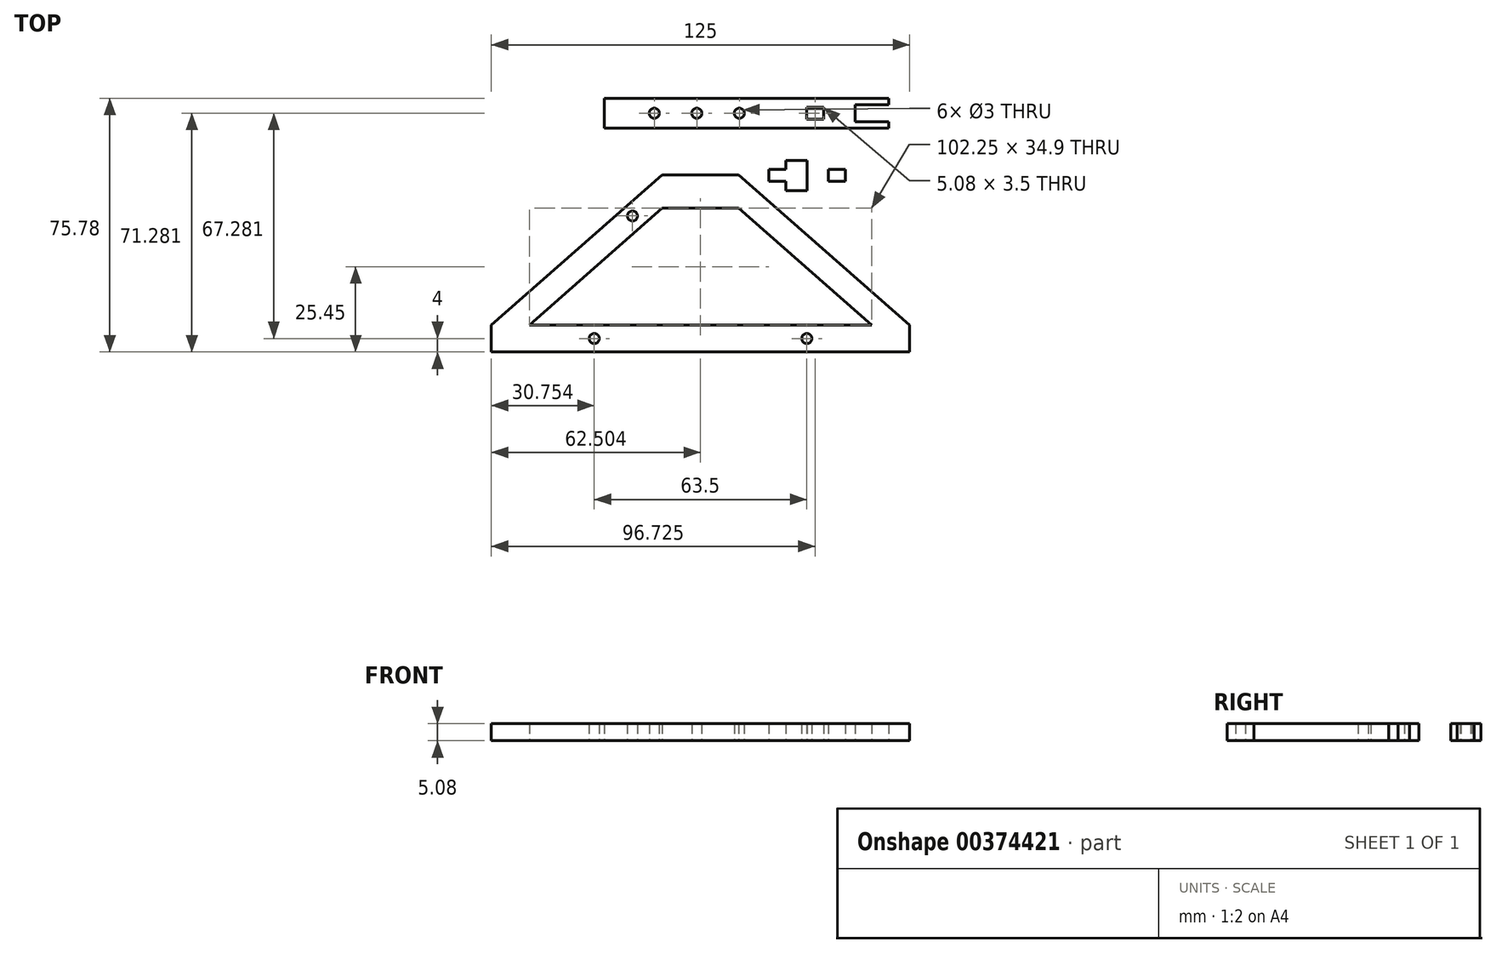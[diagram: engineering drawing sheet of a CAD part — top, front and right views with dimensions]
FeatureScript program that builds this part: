
annotation { "Feature Type Name" : "Feature", "Feature Type Description" : "" }
export const myFeature = defineFeature(function(context is Context, id is Id, definition is map)
    precondition{}
    {
        {
            var Q0;
            Q0=qCreatedBy(makeId("Top.planeOp"),FACE);
            var sketch = newSketch(context, id + "F0", { "sketchPlane" : qUnion([Q0])});
            skLineSegment(sketch, "E0.bottom", {"start": v(5, 50.75) * mm, "end": v(-80, 50.75) * mm});
            skLineSegment(sketch, "E0.top", {"start": v(5, 41.75) * mm, "end": v(-80, 41.75) * mm});
            skLineSegment(sketch, "E0.left", {"start": v(5, 50.75) * mm, "end": v(5, 41.75) * mm});
            skLineSegment(sketch, "E0.right", {"start": v(-80, 50.75) * mm, "end": v(-80, 41.75) * mm});
            skCircle(sketch, "E1", {"center": v(-65, 46.25) * mm, "radius": 1.5 * mm});
            skPoint(sketch, "E1.centerSnap0", {"position": v(-80, 46.25) * mm});
            skCircle(sketch, "E2", {"center": v(-39.6, 46.25) * mm, "radius": 1.5 * mm});
            skCircle(sketch, "E3", {"center": v(-52.3, 46.25) * mm, "radius": 1.5 * mm});
            skLineSegment(sketch, "E4.bottom", {"start": v(5, 48.8) * mm, "end": v(-5, 48.8) * mm});
            skLineSegment(sketch, "E4.top", {"start": v(5, 43.71) * mm, "end": v(-5, 43.71) * mm});
            skLineSegment(sketch, "E4.left", {"start": v(5, 48.8) * mm, "end": v(5, 43.71) * mm});
            skLineSegment(sketch, "E4.right", {"start": v(-5, 48.8) * mm, "end": v(-5, 43.71) * mm});
            skPoint(sketch, "E5.middle", {"position": v(-88.96, 46.25) * mm});
            skLineSegment(sketch, "E6.bottom", {"start": v(-19.52, 48) * mm, "end": v(-14.44, 48) * mm});
            skLineSegment(sketch, "E6.top", {"start": v(-19.52, 44.5) * mm, "end": v(-14.44, 44.5) * mm});
            skLineSegment(sketch, "E6.left", {"start": v(-19.52, 48) * mm, "end": v(-19.52, 44.5) * mm});
            skLineSegment(sketch, "E6.right", {"start": v(-14.44, 48) * mm, "end": v(-14.44, 44.5) * mm});
            skLineSegment(sketch, "E7.bottom", {"start": v(-25.75, 32.2) * mm, "end": v(-13.04, 32.2) * mm});
            skLineSegment(sketch, "E7.top", {"start": v(-25.75, 23.2) * mm, "end": v(-13.04, 23.2) * mm});
            skLineSegment(sketch, "E7.left", {"start": v(-25.75, 32.2) * mm, "end": v(-25.75, 23.2) * mm});
            skLineSegment(sketch, "E7.right", {"start": v(-13.04, 32.2) * mm, "end": v(-13.04, 23.2) * mm});
            skLineSegment(sketch, "E8.bottom", {"start": v(-13.04, 29.44) * mm, "end": v(-7.96, 29.44) * mm});
            skLineSegment(sketch, "E8.top", {"start": v(-13.04, 25.94) * mm, "end": v(-7.96, 25.94) * mm});
            skLineSegment(sketch, "E8.left", {"start": v(-13.04, 29.44) * mm, "end": v(-13.04, 25.94) * mm});
            skLineSegment(sketch, "E8.right", {"start": v(-7.96, 29.44) * mm, "end": v(-7.96, 25.94) * mm});
            skLineSegment(sketch, "E9", {"start": v(-19.4, 32.2) * mm, "end": v(-19.4, 23.2) * mm});
            skLineSegment(sketch, "E10.MirrorCS", {"start": v(-25.75, 29.44) * mm, "end": v(-30.83, 29.44) * mm});
            skLineSegment(sketch, "E11.MirrorCS", {"start": v(-30.83, 29.44) * mm, "end": v(-30.83, 25.94) * mm});
            skLineSegment(sketch, "E12.MirrorCS", {"start": v(-25.75, 25.94) * mm, "end": v(-30.83, 25.94) * mm});
            skLineSegment(sketch, "E13.bottom", {"start": v(-62.64, 27.87) * mm, "end": v(-39.77, 27.87) * mm});
            skLineSegment(sketch, "E13.top", {"start": v(-62.64, 17.87) * mm, "end": v(-39.77, 17.87) * mm});
            skLineSegment(sketch, "E13.left", {"start": v(-62.64, 27.87) * mm, "end": v(-62.64, 17.87) * mm});
            skLineSegment(sketch, "E13.right", {"start": v(-39.77, 27.87) * mm, "end": v(-39.77, 17.87) * mm});
            skLineSegment(sketch, "E14", {"start": v(-113.7, -17.03) * mm, "end": v(11.3, -17.03) * mm});
            skLineSegment(sketch, "E15", {"start": v(-113.7, -17.03) * mm, "end": v(-113.7, -25.03) * mm});
            skLineSegment(sketch, "E16", {"start": v(-113.7, -25.03) * mm, "end": v(11.3, -25.03) * mm});
            skLineSegment(sketch, "E17", {"start": v(11.3, -25.03) * mm, "end": v(11.3, -17.03) * mm});
            skCircle(sketch, "E18", {"center": v(-82.96, -21.03) * mm, "radius": 1.5 * mm});
            skPoint(sketch, "E18.centerSnap0", {"position": v(-113.7, -21.03) * mm});
            skCircle(sketch, "E19", {"center": v(-19.46, -21.03) * mm, "radius": 1.5 * mm});
            skLineSegment(sketch, "E20", {"start": v(-113.7, -17.03) * mm, "end": v(-62.64, 27.87) * mm});
            skLineSegment(sketch, "E21", {"start": v(-62.64, 17.87) * mm, "end": v(-102.33, -17.03) * mm});
            skLineSegment(sketch, "E22", {"start": v(-51.2, 27.87) * mm, "end": v(-51.2, -25.03) * mm});
            skLineSegment(sketch, "E23.MirrorCS", {"start": v(11.3, -17.03) * mm, "end": v(-39.77, 27.87) * mm});
            skLineSegment(sketch, "E24.MirrorCS", {"start": v(-39.77, 17.87) * mm, "end": v(-0.08, -17.03) * mm});
            skCircle(sketch, "E25", {"center": v(-71.53, 15.58) * mm, "radius": 1.5 * mm});
            skLineSegment(sketch, "E26", {"start": v(-62.64, 22.87) * mm, "end": v(-71.53, 15.58) * mm});
            skSolve(sketch);
        }
        {
            var Q0;
            Q0=makeQuery(id+"F0.imprint","IMPRINT",FACE,{"disambiguationData":[TD([[makeQuery(id+"F0.imprint","IMPRINT",EDGE,{"derivedFrom":sQuery(id+"F0.wireOp",EDGE,"E0.bottom")}),1.0]])]});
            var Q1;
            {var subQ6=sQuery(id+"F0.wireOp",EDGE,"E9");Q1=makeQuery(id+"F0.imprint","IMPRINT",FACE,{"disambiguationData":[TD([[makeQuery(id+"F0.imprint","IMPRINT",EDGE,{"derivedFrom":subQ6}),-1.0]])]});}
            var Q2;
            {var subQ0=sQuery(id+"F0.wireOp",EDGE,"E10.MirrorCS");Q2=makeQuery(id+"F0.imprint","IMPRINT",FACE,{"disambiguationData":[TD([[makeQuery(id+"F0.imprint","IMPRINT",EDGE,{"derivedFrom":subQ0}),1.0]])]});}
            var Q3;
            {var subQ3=sQuery(id+"F0.wireOp",EDGE,"E8.left");Q3=makeQuery(id+"F0.imprint","IMPRINT",FACE,{"disambiguationData":[TD([[makeQuery(id+"F0.imprint","IMPRINT",EDGE,{"derivedFrom":subQ3}),-1.0]])]});}
            var Q4;
            Q4=makeQuery(id+"F0.imprint","IMPRINT",FACE,{"disambiguationData":[TD([[makeQuery(id+"F0.imprint","IMPRINT",EDGE,{"derivedFrom":sQuery(id+"F0.wireOp",EDGE,"E8.bottom")}),-1.0]])]});
            var Q5;
            Q5=makeQuery(id+"F0.imprint","IMPRINT",FACE,{"disambiguationData":[TD([[makeQuery(id+"F0.imprint","IMPRINT",EDGE,{"derivedFrom":sQuery(id+"F0.wireOp",EDGE,"E13.bottom")}),-1.0]])]});
            var Q6;
            Q6=makeQuery(id+"F0.imprint","IMPRINT",FACE,{"disambiguationData":[TD([[makeQuery(id+"F0.imprint","IMPRINT",EDGE,{"derivedFrom":sQuery(id+"F0.wireOp",EDGE,"acEFhCEI-yFbl-H2Pa-5wQp-K0OgbWs3FAEt.top")}),1.0]])]});
            var Q7;
            {var subQ0=sQuery(id+"F0.wireOp",EDGE,"dQzkJBef-Vm0C-bMXC-JUuQ-Ov79O9Y2UqkZ");Q7=makeQuery(id+"F0.imprint","IMPRINT",FACE,{"disambiguationData":[TD([[makeQuery(id+"F0.imprint","IMPRINT",EDGE,{"derivedFrom":subQ0}),-1.0]])]});}
            var Q8;
            {var subQ0=sQuery(id+"F0.wireOp",EDGE,"E13.left");Q8=makeQuery(id+"F0.imprint","IMPRINT",FACE,{"disambiguationData":[TD([[makeQuery(id+"F0.imprint","IMPRINT",EDGE,{"derivedFrom":subQ0}),-1.0]])]});}
            var Q9;
            {var subQ0=sQuery(id+"F0.wireOp",EDGE,"E13.right");Q9=makeQuery(id+"F0.imprint","IMPRINT",FACE,{"disambiguationData":[TD([[makeQuery(id+"F0.imprint","IMPRINT",EDGE,{"derivedFrom":subQ0}),1.0]])]});}
            var Q10;
            {var subQ0=sQuery(id+"F0.wireOp",EDGE,"e530f1da-0833-4975-b5ee-6b59f7a18dae0.MirrorCS");Q10=makeQuery(id+"F0.imprint","IMPRINT",FACE,{"disambiguationData":[TD([[makeQuery(id+"F0.imprint","IMPRINT",EDGE,{"derivedFrom":subQ0}),1.0]])]});}
            var Q11;
            {var subQ0=sQuery(id+"F0.wireOp",EDGE,"E15");Q11=makeQuery(id+"F0.imprint","IMPRINT",FACE,{"disambiguationData":[TD([[makeQuery(id+"F0.imprint","IMPRINT",EDGE,{"derivedFrom":subQ0}),1.0]])]});}
            var Q12;
            {var subQ0=sQuery(id+"F0.wireOp",EDGE,"E17");Q12=makeQuery(id+"F0.imprint","IMPRINT",FACE,{"disambiguationData":[TD([[makeQuery(id+"F0.imprint","IMPRINT",EDGE,{"derivedFrom":subQ0}),1.0]])]});}
            var Q13;
            {var subQ0=sQuery(id+"F0.wireOp",EDGE,"E13.left");var subQ3=makeQuery(id+"F0.imprint","IMPRINT",VERTEX,{"derivedFrom":subQ0});Q13=makeQuery(id+"F0.imprint","IMPRINT",FACE,{"disambiguationData":[TD([[makeQuery(id+"F0.imprint","IMPRINT",EDGE,{"disambiguationData":[TD([[subQ3,1.0]])],"derivedFrom":subQ0}),1.0]])]});}
            extrude(context, id + "F1", {"entities" : qUnion([Q0, Q1, Q2, Q3, Q4, Q5, Q6, Q7, Q8, Q9, Q10, Q11, Q12, Q13]), "depth" : 5.08 * mm});
        }
    });
